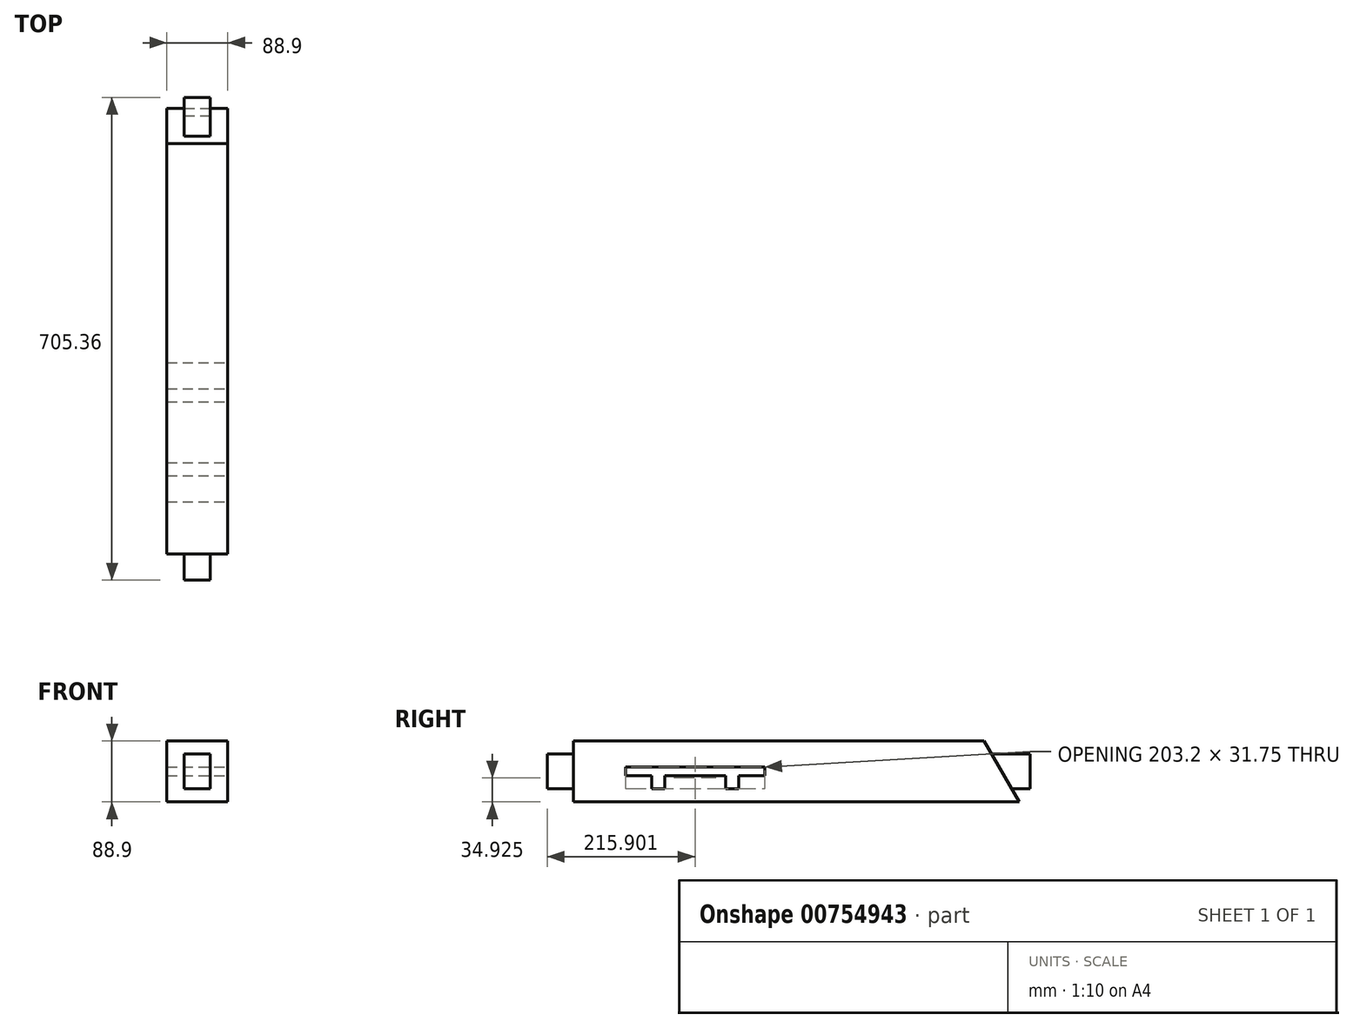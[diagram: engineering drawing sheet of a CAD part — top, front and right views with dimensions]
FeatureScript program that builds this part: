
annotation { "Feature Type Name" : "Feature", "Feature Type Description" : "" }
export const myFeature = defineFeature(function(context is Context, id is Id, definition is map)
    precondition{}
    {
        {
            var Q0;
            Q0=qCreatedBy(makeId("Right.planeOp"),FACE);
            var sketch = newSketch(context, id + "F0", { "sketchPlane" : qUnion([Q0])});
            skLineSegment(sketch, "E0.bottom", {"start": v(-352.68, 44.45) * mm, "end": v(352.68, 44.45) * mm});
            skLineSegment(sketch, "E0.top", {"start": v(-352.68, -44.45) * mm, "end": v(352.68, -44.45) * mm});
            skLineSegment(sketch, "E0.left", {"start": v(-352.68, 44.45) * mm, "end": v(-352.68, -44.45) * mm});
            skLineSegment(sketch, "E0.right", {"start": v(352.68, 44.45) * mm, "end": v(352.68, -44.45) * mm});
            skPoint(sketch, "E0.middle", {"position": v(0, 0) * mm});
            skSolve(sketch);
        }
        {
            var Q0;
            Q0 = qSketchRegion(id + "F0", true);
            extrude(context, id + "F1", {"entities" : qUnion([Q0]), "endBound" : BoundingType.SYMMETRIC, "depth" : 88.9 * mm, "offsetDistance" : 25.4 * mm});
        }
        {
            var Q0;
            Q0=makeQuery(id+"F1.opExtrude","SWEPT_FACE",FACE,{"disambiguationData":[OSD([sQuery(id+"F0.wireOp",EDGE,"E0.bottom")])]});
            var sketch = newSketch(context, id + "F2", { "sketchPlane" : qUnion([Q0])});
            skLineSegment(sketch, "E1", {"start": v(-44.45, 285.12) * mm, "end": v(44.45, 285.12) * mm, "construction": true});
            skSolve(sketch);
        }
        {
            var Q0;
            Q0=sQuery(id+"F2.wireOp",EDGE,"E1");
            cPlane(context, id + "F3", {"entities" : qUnion([Q0]), "cplaneType" : CPlaneType.LINE_ANGLE, "offset" : 25.4 * mm, "angle" : 30 * degree, "width" : 152.4 * mm, "height" : 152.4 * mm});
        }
        {
            var Q0;
            Q0=makeQuery(id+"F1.opExtrude","SWEPT_FACE",FACE,{"disambiguationData":[OSD([sQuery(id+"F0.wireOp",EDGE,"E0.right")])]});
            var sketch = newSketch(context, id + "F4", { "sketchPlane" : qUnion([Q0])});
            skLineSegment(sketch, "E2.bottom", {"start": v(-19.05, 25.4) * mm, "end": v(19.05, 25.4) * mm});
            skLineSegment(sketch, "E2.top", {"start": v(-19.05, -25.4) * mm, "end": v(19.05, -25.4) * mm});
            skLineSegment(sketch, "E2.left", {"start": v(-19.05, 25.4) * mm, "end": v(-19.05, -25.4) * mm});
            skLineSegment(sketch, "E2.right", {"start": v(19.05, 25.4) * mm, "end": v(19.05, -25.4) * mm});
            skPoint(sketch, "E2.middle", {"position": v(0, 0) * mm});
            skLineSegment(sketch, "E3.bottom", {"start": v(-44.45, 44.45) * mm, "end": v(44.45, 44.45) * mm});
            skLineSegment(sketch, "E3.top", {"start": v(-44.45, -44.45) * mm, "end": v(44.45, -44.45) * mm});
            skLineSegment(sketch, "E3.left", {"start": v(-44.45, 44.45) * mm, "end": v(-44.45, -44.45) * mm});
            skLineSegment(sketch, "E3.right", {"start": v(44.45, 44.45) * mm, "end": v(44.45, -44.45) * mm});
            skSolve(sketch);
        }
        {
            var Q0;
            Q0 = qSketchRegion(id + "F4", true);
            var Q1;
            Q1=qCreatedBy(id+"F3.planeOp",FACE);
            extrude(context, id + "F5", {"entities" : qUnion([Q0]), "operationType" : NewBodyOperationType.REMOVE, "endBound" : BoundingType.UP_TO_SURFACE, "oppositeDirection" : true, "depth" : 25.4 * mm, "endBoundEntityFace" : qUnion([Q1]), "offsetDistance" : 25.4 * mm});
        }
        {
            var Q0;
            Q0=makeQuery(id+"F1.opExtrude","SWEPT_FACE",FACE,{"disambiguationData":[OSD([sQuery(id+"F0.wireOp",EDGE,"E0.left")])]});
            var sketch = newSketch(context, id + "F6", { "sketchPlane" : qUnion([Q0])});
            skLineSegment(sketch, "E4.bottom", {"start": v(-44.45, 44.45) * mm, "end": v(44.45, 44.45) * mm});
            skLineSegment(sketch, "E4.top", {"start": v(-44.45, -44.45) * mm, "end": v(44.45, -44.45) * mm});
            skLineSegment(sketch, "E4.left", {"start": v(-44.45, 44.45) * mm, "end": v(-44.45, -44.45) * mm});
            skLineSegment(sketch, "E4.right", {"start": v(44.45, 44.45) * mm, "end": v(44.45, -44.45) * mm});
            skPoint(sketch, "E4.middle", {"position": v(0, 0) * mm});
            skLineSegment(sketch, "E5.bottom", {"start": v(-19.05, 25.4) * mm, "end": v(19.05, 25.4) * mm});
            skLineSegment(sketch, "E5.top", {"start": v(-19.05, -25.4) * mm, "end": v(19.05, -25.4) * mm});
            skLineSegment(sketch, "E5.left", {"start": v(-19.05, 25.4) * mm, "end": v(-19.05, -25.4) * mm});
            skLineSegment(sketch, "E5.right", {"start": v(19.05, 25.4) * mm, "end": v(19.05, -25.4) * mm});
            skSolve(sketch);
        }
        {
            var Q0;
            Q0 = qSketchRegion(id + "F6", true);
            extrude(context, id + "F7", {"entities" : qUnion([Q0]), "operationType" : NewBodyOperationType.REMOVE, "oppositeDirection" : true, "depth" : 38.1 * mm, "offsetDistance" : 25.4 * mm});
        }
        {
            var Q0;
            Q0=makeQuery(id+"F1.opExtrude","CAP_FACE",FACE,{"disambiguationData":[OSD([sQuery(id+"F0.wireOp",EDGE,"E0.bottom"),sQuery(id+"F0.wireOp",EDGE,"E0.top"),sQuery(id+"F0.wireOp",EDGE,"E0.left"),sQuery(id+"F0.wireOp",EDGE,"E0.right")])],"isStart":false});
            var sketch = newSketch(context, id + "F8", { "sketchPlane" : qUnion([Q0])});
            skLineSegment(sketch, "E6.bottom", {"start": v(-35.18, 6.35) * mm, "end": v(-238.38, 6.35) * mm});
            skLineSegment(sketch, "E6.top", {"start": v(-35.18, -6.35) * mm, "end": v(-73.28, -6.35) * mm});
            skLineSegment(sketch, "E6.left", {"start": v(-35.18, 6.35) * mm, "end": v(-35.18, -6.35) * mm});
            skLineSegment(sketch, "E6.right", {"start": v(-238.38, 6.35) * mm, "end": v(-238.38, -6.35) * mm});
            skPoint(sketch, "E6.middle", {"position": v(-136.78, 0) * mm});
            skLineSegment(sketch, "E7", {"start": v(-200.28, -6.35) * mm, "end": v(-200.28, -25.4) * mm});
            skLineSegment(sketch, "E8", {"start": v(-200.28, -25.4) * mm, "end": v(-181.23, -25.4) * mm});
            skLineSegment(sketch, "E9", {"start": v(-181.23, -25.4) * mm, "end": v(-181.23, -6.35) * mm});
            skLineSegment(sketch, "E10", {"start": v(-92.33, -6.35) * mm, "end": v(-92.33, -25.4) * mm});
            skLineSegment(sketch, "E11", {"start": v(-92.33, -25.4) * mm, "end": v(-73.28, -25.4) * mm});
            skLineSegment(sketch, "E12", {"start": v(-73.28, -25.4) * mm, "end": v(-73.28, -6.35) * mm});
            skLineSegment(sketch, "E13.trimOffspring", {"start": v(-200.28, -6.35) * mm, "end": v(-238.38, -6.35) * mm});
            skLineSegment(sketch, "E14.trimOffspring", {"start": v(-92.33, -6.35) * mm, "end": v(-181.23, -6.35) * mm});
            skSolve(sketch);
        }
        {
            var Q0;
            Q0 = qSketchRegion(id + "F8", true);
            extrude(context, id + "F9", {"entities" : qUnion([Q0]), "operationType" : NewBodyOperationType.REMOVE, "endBound" : BoundingType.THROUGH_ALL, "oppositeDirection" : true, "depth" : 25.4 * mm, "offsetDistance" : 25.4 * mm});
        }
    });
